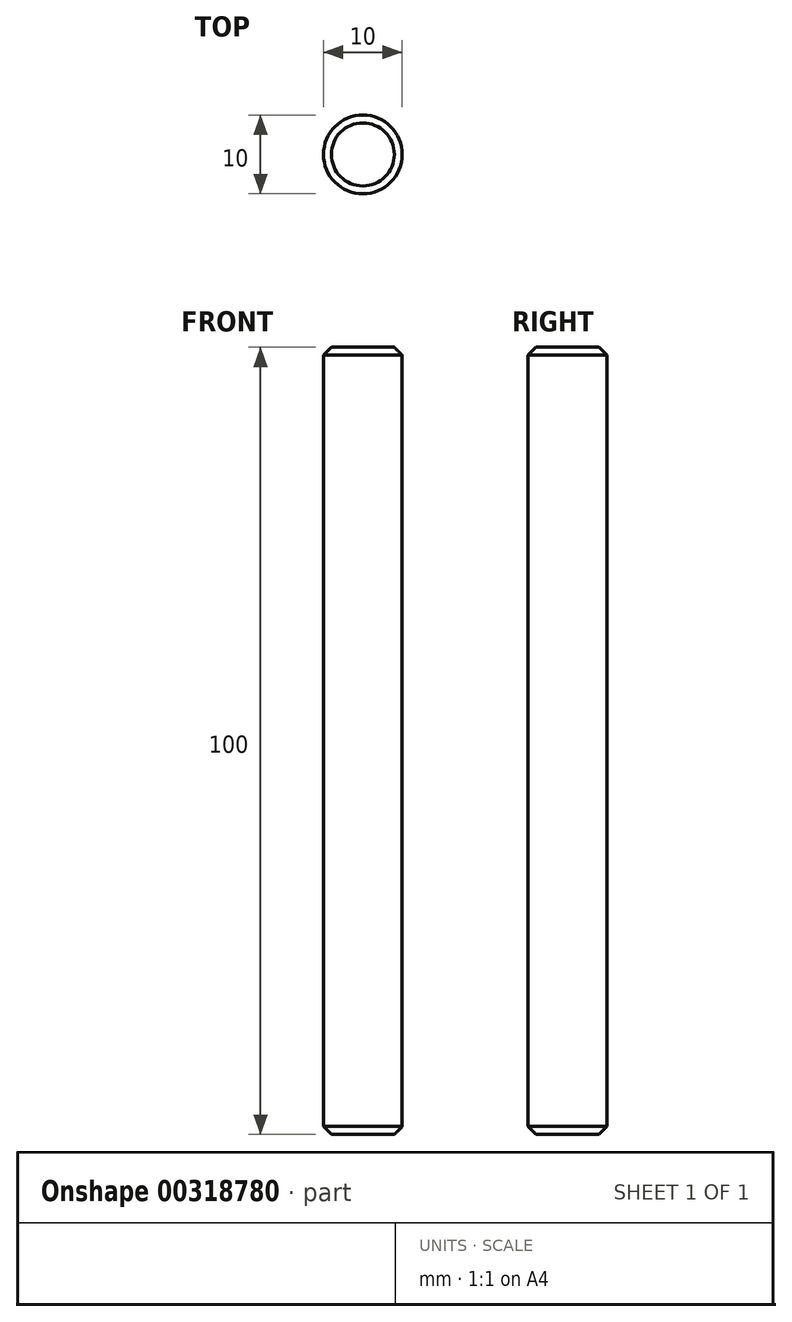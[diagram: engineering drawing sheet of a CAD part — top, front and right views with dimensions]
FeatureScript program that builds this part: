
annotation { "Feature Type Name" : "Feature", "Feature Type Description" : "" }
export const myFeature = defineFeature(function(context is Context, id is Id, definition is map)
    precondition{}
    {
        {
            var Q0;
            Q0=qCreatedBy(makeId("Top.planeOp"),FACE);
            var sketch = newSketch(context, id + "F0", { "sketchPlane" : qUnion([Q0])});
            skCircle(sketch, "E0", {"center": v(0, 0) * mm, "radius": 5 * mm});
            skSolve(sketch);
        }
        {
            var Q0;
            Q0 = qSketchRegion(id + "F0", true);
            extrude(context, id + "F1", {"entities" : qUnion([Q0]), "depth" : 100 * mm, "offsetDistance" : 25 * mm});
        }
        {
            var Q0;
            Q0=makeQuery(id+"F1.opExtrude","CAP_FACE",FACE,{"disambiguationData":[OSD([sQuery(id+"F0.wireOp",EDGE,"E0")])],"isStart":false});
            var Q1;
            Q1=makeQuery(id+"F1.opExtrude","CAP_FACE",FACE,{"disambiguationData":[OSD([sQuery(id+"F0.wireOp",EDGE,"E0")])],"isStart":true});
            chamfer(context, id + "F2", {"entities" : qUnion([Q0, Q1]), "width" : 1 * mm, "tangentPropagation" : true});
        }
    });
